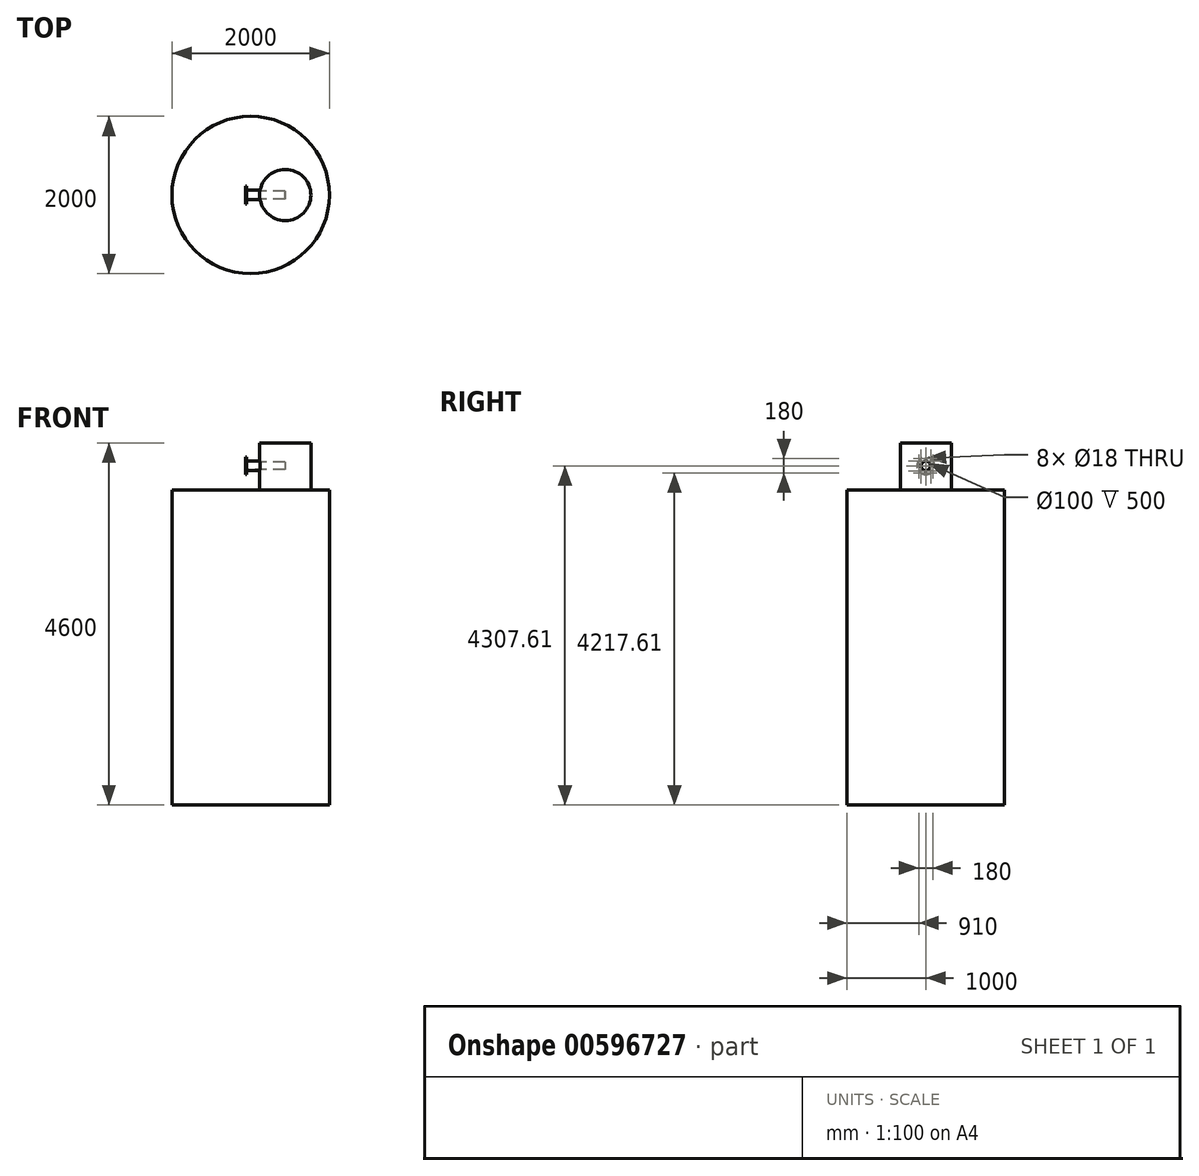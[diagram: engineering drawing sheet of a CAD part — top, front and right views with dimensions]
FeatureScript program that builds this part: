
annotation { "Feature Type Name" : "Feature", "Feature Type Description" : "" }
export const myFeature = defineFeature(function(context is Context, id is Id, definition is map)
    precondition{}
    {
        {
            var Q0;
            Q0=qCreatedBy(makeId("Top.planeOp"),FACE);
            var sketch = newSketch(context, id + "F0", { "sketchPlane" : qUnion([Q0])});
            skCircle(sketch, "E0", {"center": v(0, 0) * mm, "radius": 1000 * mm});
            skSolve(sketch);
        }
        {
            var Q0;
            Q0=makeQuery(id+"F0.imprint","IMPRINT",FACE,{"disambiguationData":[TD([[makeQuery(id+"F0.imprint","IMPRINT",EDGE,{"derivedFrom":sQuery(id+"F0.wireOp",EDGE,"E0")}),1.0]])]});
            extrude(context, id + "F1", {"entities" : qUnion([Q0]), "depth" : 4000 * mm, "offsetDistance" : 25 * mm});
        }
        {
            var Q0;
            Q0=makeQuery(id+"F1.opExtrude","CAP_FACE",FACE,{"disambiguationData":[OSD([sQuery(id+"F0.wireOp",EDGE,"E0")])],"isStart":false});
            var sketch = newSketch(context, id + "F2", { "sketchPlane" : qUnion([Q0])});
            skCircle(sketch, "E1", {"center": v(439.88, 0) * mm, "radius": 325 * mm});
            skSolve(sketch);
        }
        {
            var Q0;
            Q0=makeQuery(id+"F2.imprint","IMPRINT",FACE,{"disambiguationData":[TD([[makeQuery(id+"F2.imprint","IMPRINT",EDGE,{"derivedFrom":sQuery(id+"F2.wireOp",EDGE,"E1")}),1.0]])]});
            extrude(context, id + "F3", {"entities" : qUnion([Q0]), "operationType" : NewBodyOperationType.ADD, "depth" : 600 * mm, "offsetDistance" : 25 * mm});
        }
        {
            var Q0;
            Q0=qCreatedBy(makeId("Right.planeOp"),FACE);
            cPlane(context, id + "F4", {"entities" : qUnion([Q0]), "cplaneType" : CPlaneType.OFFSET, "offset" : 200 * mm, "width" : 150 * mm, "height" : 150 * mm});
        }
        {
            var Q0;
            Q0=qCreatedBy(id+"F4.planeOp",FACE);
            var sketch = newSketch(context, id + "F5", { "sketchPlane" : qUnion([Q0])});
            skCircle(sketch, "E2", {"center": v(0, 4307.61) * mm, "radius": 60 * mm});
            skSolve(sketch);
        }
        {
            var Q0;
            Q0 = qSketchRegion(id + "F5", true);
            extrude(context, id + "F6", {"entities" : qUnion([Q0]), "operationType" : NewBodyOperationType.ADD, "oppositeDirection" : true, "depth" : 250 * mm, "offsetDistance" : 25 * mm});
        }
        {
            var Q0;
            Q0=makeQuery(id+"F6.opExtrude","CAP_FACE",FACE,{"disambiguationData":[OSD([sQuery(id+"F5.wireOp",EDGE,"E2")])],"isStart":false});
            var sketch = newSketch(context, id + "F7", { "sketchPlane" : qUnion([Q0])});
            skCircle(sketch, "E3", {"center": v(0, 4307.61) * mm, "radius": 112.5 * mm});
            skSolve(sketch);
        }
        {
            var Q0;
            Q0=makeQuery(id+"F7.imprint","IMPRINT",FACE,{"disambiguationData":[TD([[makeQuery(id+"F7.imprint","IMPRINT",EDGE,{"derivedFrom":sQuery(id+"F7.wireOp",EDGE,"E3")}),1.0]])]});
            var Q1;
            Q1=makeQuery(id+"F7.imprint","IMPRINT",FACE,{"disambiguationData":[TD([[makeQuery(id+"F7.imprint","IMPRINT",EDGE,{"derivedFrom":makeQuery(id+"F6.opExtrude","CAP_EDGE",EDGE,{"disambiguationData":[OSD([sQuery(id+"F5.wireOp",EDGE,"E2")])],"isStart":false})}),-1.0]])]});
            var Q2;
            Q2=sQuery(id+"F7.wireOp",EDGE,"E3");
            extrude(context, id + "F8", {"entities" : qUnion([Q0, Q1]), "operationType" : NewBodyOperationType.ADD, "surfaceEntities" : qUnion([Q2]), "depth" : 15 * mm, "offsetDistance" : 25 * mm});
        }
        {
            var Q0;
            Q0=makeQuery(id+"F8.opExtrude","CAP_FACE",FACE,{"disambiguationData":[OSD([sQuery(id+"F7.wireOp",EDGE,"E3")])],"isStart":false});
            var sketch = newSketch(context, id + "F9", { "sketchPlane" : qUnion([Q0])});
            skCircle(sketch, "E4", {"center": v(0, 4307.61) * mm, "radius": 50 * mm});
            skSolve(sketch);
        }
        {
            var Q0;
            Q0=makeQuery(id+"F9.imprint","IMPRINT",FACE,{"disambiguationData":[TD([[makeQuery(id+"F9.imprint","IMPRINT",EDGE,{"derivedFrom":sQuery(id+"F9.wireOp",EDGE,"E4")}),1.0]])]});
            extrude(context, id + "F10", {"entities" : qUnion([Q0]), "operationType" : NewBodyOperationType.REMOVE, "oppositeDirection" : true, "depth" : 500 * mm, "offsetDistance" : 25 * mm});
        }
        {
            var Q0;
            Q0=makeQuery(id+"F8.opExtrude","CAP_FACE",FACE,{"disambiguationData":[OSD([sQuery(id+"F7.wireOp",EDGE,"E3")])],"isStart":false});
            var sketch = newSketch(context, id + "F11", { "sketchPlane" : qUnion([Q0])});
            skCircle(sketch, "E5", {"center": v(0, 4397.61) * mm, "radius": 9 * mm});
            skCircle(sketch, "E6.1.0", {"center": v(-63.64, 4371.25) * mm, "radius": 9 * mm});
            skCircle(sketch, "E6.2.0", {"center": v(-90, 4307.61) * mm, "radius": 9 * mm});
            skCircle(sketch, "E6.3.0", {"center": v(-63.64, 4243.97) * mm, "radius": 9 * mm});
            skCircle(sketch, "E6.4.0", {"center": v(0, 4217.61) * mm, "radius": 9 * mm});
            skCircle(sketch, "E6.5.0", {"center": v(63.64, 4243.97) * mm, "radius": 9 * mm});
            skCircle(sketch, "E6.6.0", {"center": v(90, 4307.61) * mm, "radius": 9 * mm});
            skCircle(sketch, "E6.7.0", {"center": v(63.64, 4371.25) * mm, "radius": 9 * mm});
            skPoint(sketch, "E6.center", {"position": v(0, 4307.61) * mm});
            skSolve(sketch);
        }
        {
            var Q0;
            Q0=makeQuery(id+"F11.imprint","IMPRINT",FACE,{"disambiguationData":[TD([[makeQuery(id+"F11.imprint","IMPRINT",EDGE,{"derivedFrom":sQuery(id+"F11.wireOp",EDGE,"E5")}),1.0]])]});
            var Q1;
            Q1=makeQuery(id+"F11.imprint","IMPRINT",FACE,{"disambiguationData":[TD([[makeQuery(id+"F11.imprint","IMPRINT",EDGE,{"derivedFrom":sQuery(id+"F11.wireOp",EDGE,"E6.1.0")}),1.0]])]});
            var Q2;
            Q2=makeQuery(id+"F11.imprint","IMPRINT",FACE,{"disambiguationData":[TD([[makeQuery(id+"F11.imprint","IMPRINT",EDGE,{"derivedFrom":sQuery(id+"F11.wireOp",EDGE,"E6.2.0")}),1.0]])]});
            var Q3;
            Q3=makeQuery(id+"F11.imprint","IMPRINT",FACE,{"disambiguationData":[TD([[makeQuery(id+"F11.imprint","IMPRINT",EDGE,{"derivedFrom":sQuery(id+"F11.wireOp",EDGE,"E6.3.0")}),1.0]])]});
            var Q4;
            Q4=makeQuery(id+"F11.imprint","IMPRINT",FACE,{"disambiguationData":[TD([[makeQuery(id+"F11.imprint","IMPRINT",EDGE,{"derivedFrom":sQuery(id+"F11.wireOp",EDGE,"E6.4.0")}),1.0]])]});
            var Q5;
            Q5=makeQuery(id+"F11.imprint","IMPRINT",FACE,{"disambiguationData":[TD([[makeQuery(id+"F11.imprint","IMPRINT",EDGE,{"derivedFrom":sQuery(id+"F11.wireOp",EDGE,"E6.5.0")}),1.0]])]});
            var Q6;
            Q6=makeQuery(id+"F11.imprint","IMPRINT",FACE,{"disambiguationData":[TD([[makeQuery(id+"F11.imprint","IMPRINT",EDGE,{"derivedFrom":sQuery(id+"F11.wireOp",EDGE,"E6.6.0")}),1.0]])]});
            var Q7;
            Q7=makeQuery(id+"F11.imprint","IMPRINT",FACE,{"disambiguationData":[TD([[makeQuery(id+"F11.imprint","IMPRINT",EDGE,{"derivedFrom":sQuery(id+"F11.wireOp",EDGE,"E6.7.0")}),1.0]])]});
            extrude(context, id + "F12", {"entities" : qUnion([Q0, Q1, Q2, Q3, Q4, Q5, Q6, Q7]), "operationType" : NewBodyOperationType.REMOVE, "oppositeDirection" : true, "depth" : 25 * mm, "offsetDistance" : 25 * mm});
        }
    });
